# Revit family: NBS_TapcoRoofingProducts_RcnstttdSltCrsngFitngs_DaVinciSelectShakeRidgeAndHipCap
name_source: partatom
category: Generic Models
units: mm (PartAtom-declared; Revit-internal decimal feet)

## family parameters
Can host rebar = No
Cut with Voids When Loaded = No
Part Type = Normal
Room Calculation Point = No
Round Connector Dimension = Use Diameter
Shared = No

## types (3) — shared parameters
AssetType = Fixed
BackThickness = 3 mm  [stored 0.00984252 ft]
Category = Pr_35_90_93_29:Dry fixing ridges
CodePerformance = To EN 13501-5, BROOF(t4); Hail rating Class 4 UL 2218
Color = Black,Brown
Construction = Composite blend of virgin polyethylene, UV and thermal stabilizers as well as a highly specialized fire retardant
CountryOfMaterialOrigin = United States
CountryOfProductManufacture = United States
Description = A dry-fix ridge and hip cap for all roofs
Dimensions = 302 x 465 mm
DurationUnit = year
Features = Ridges and hips are mechanically fixed, choice of three colours to match the Select Shake tiles, fully tested to BBA standards, including fire rating, wind, driven snow and rain, and water absorption
Finish = Woodgrain
FireRating = To EN 13501-5, BROOF(t4)
Form = Duo-ridge unventilated dry fixing kits
FrontThickness = 25 mm  [stored 0.082021 ft]
IfcExportAs = IfcCoveringType
IfcExportType = ROOFING
ManufacturerName = Tapco Roofing Products
ManufacturerURL = www.tapcoroofingproducts.com
ModelReference = DaVinci Select Shake Ridge and Hip Caps
NBSInstanceId = 8821bbdf-7cdb-445a-bb53-3dfe837d31da
NBSObjectId = 5f42ca6f-9695-4291-a67d-1041d41023c2
NominalLength = 465 mm  [stored 1.52559 ft]
NominalWidth = 302 mm  [stored 0.990814 ft]
ProductInformation = https://source.thenbs.com
Recyclability = Manufactured from recyclable virgin polyethylene
RecycledContent = 0
RidgeLength = 465 mm  [stored 1.52559 ft]
Shape = Other
Size = 465 x 302 mm
SustainabilityPerformance = Manufactured from recyclable virgin polyethylene
Thickness = 25 mm  [stored 0.082021 ft]
Uniclass2015Code = Pr_35_90_93_29
Uniclass2015Title = Dry fixing ridges
Uniclass2015Version = Products v1.29
Version = 2
WarrantyDescription = 40 year
WarrantyDurationUnit = year
Weight = 1 kg
Width = 300 mm
WidthBack = 250 mm  [stored 0.82021 ft]
zero-valued in all types: Default Elevation, NominalHeight

## per-type parameters (varying)
| type | BIMObjectName | Colour | NBSVariantId | Name | RidgeMaterial |
| AgedCedar | NBS_TapcoRoofingProducts_DryFixingRidges_DaVinciSelectShakeRidge&HipCaps_AgedCedar | Aged cedar | e01b2727-56a0-ac81-1c7b-a2fdbdb3b848 | DryFixingRidges_DaVinciSelectShakeRidgeAndHipCaps_AgedCedar_TapcoRoofingProducts | NBS_TapcoRoofingProducts_AgedCedar |
| BlackOak | NBS_TapcoRoofingProducts_DryFixingRidges_DaVinciSelectShakeRidge&HipCaps_BlackOak | Black oak | c9265ae5-8019-caef-6ea6-5db136d68210 | DryFixingRidges_DaVinciSelectShakeRidgeAndHipCaps_BlackOak_TapcoRoofingProducts | NBS_TapcoRoofingProducts_BlackOak |
| Autumn | NBS_TapcoRoofingProducts_DryFixingRidges_DaVinciSelectShakeRidge&HipCaps_Autumn | Autumn | 5a28dfd7-20bb-93d9-d1d7-ee850a88a3fa | DryFixingRidges_DaVinciSelectShakeRidgeAndHipCaps_Autumn_TapcoRoofingProducts | NBS_TapcoRoofingProducts_Autumn |

note: [stored X ft] marks values corroborated as IEEE doubles in the binary element streams (Revit-internal decimal feet)

## geometry (parser evidence)
native form markers: Sweep x5
no freeform markers — native parametric forms only
